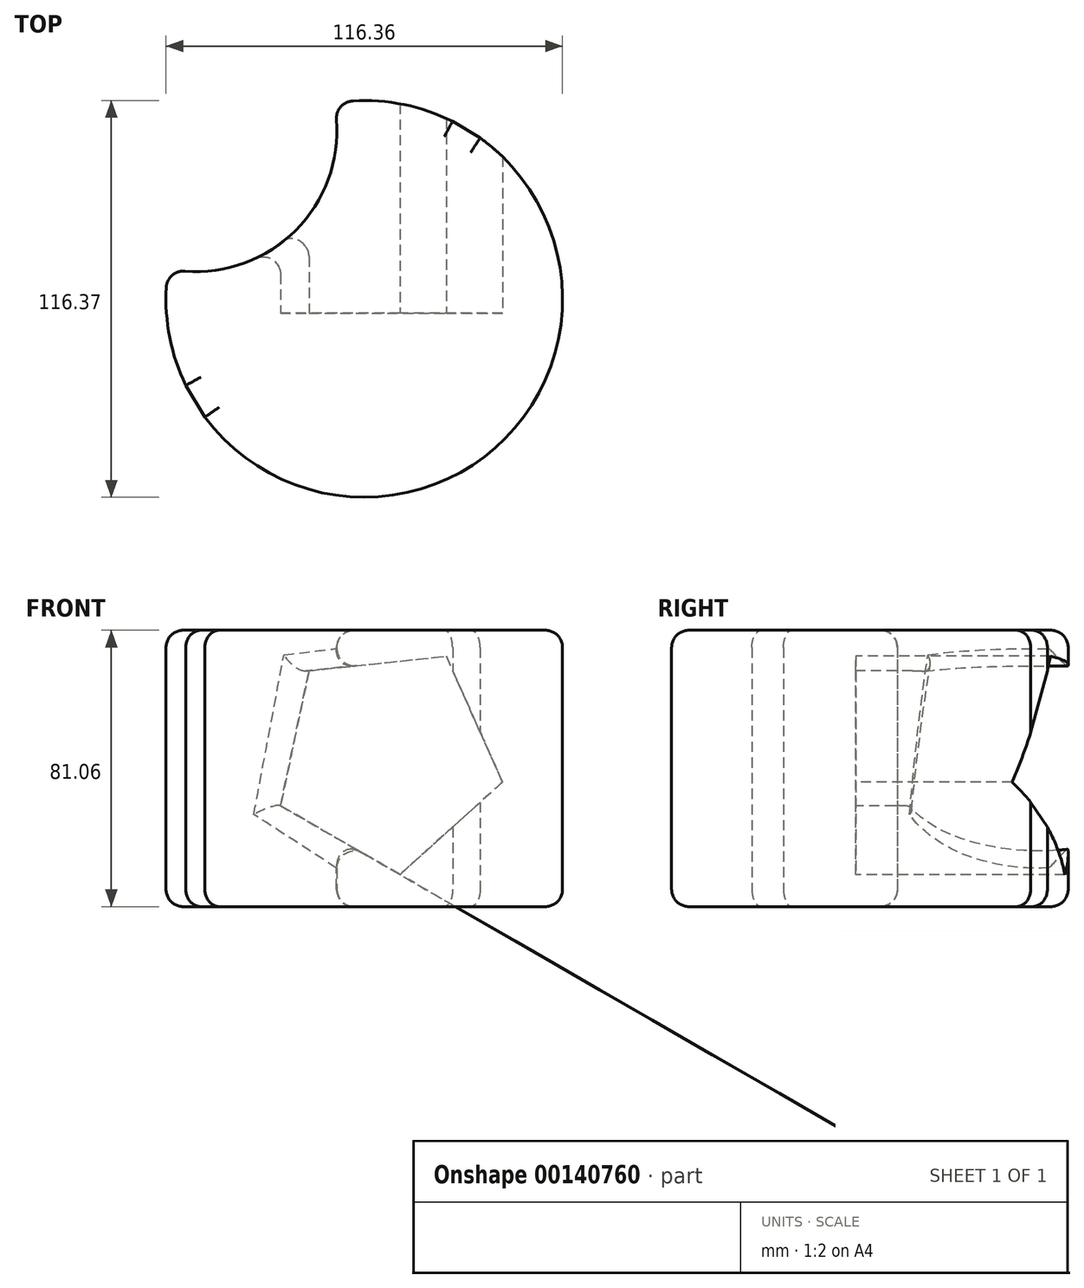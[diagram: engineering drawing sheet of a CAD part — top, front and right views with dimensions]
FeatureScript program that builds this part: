
annotation { "Feature Type Name" : "Feature", "Feature Type Description" : "" }
export const myFeature = defineFeature(function(context is Context, id is Id, definition is map)
    precondition{}
    {
        {
            var Q0;
            Q0=qCreatedBy(makeId("Top.planeOp"),FACE);
            var sketch = newSketch(context, id + "F0", { "sketchPlane" : qUnion([Q0])});
            skCircle(sketch, "E0", {"center": v(-56.15, 53.49) * mm, "radius": 41.28 * mm});
            skCircle(sketch, "E1", {"center": v(-6.85, 4.17) * mm, "radius": 58.18 * mm});
            skLineSegment(sketch, "E2", {"start": v(-33.36, 87.91) * mm, "end": v(27.16, 51.37) * mm});
            skLineSegment(sketch, "E3", {"start": v(-91.43, 32.05) * mm, "end": v(-53.6, -30.47) * mm});
            skSolve(sketch);
        }
        {
            var Q0;
            {var subQ1=sQuery(id+"F0.wireOp",EDGE,"E1");var subQ6=sQuery(id+"F0.wireOp",EDGE,"E0");var subQ9=makeQuery(id+"F0.imprint","INTERSECT",VERTEX,{"disambiguationData":[OD(0.0)],"derivedFrom":[subQ6,subQ1]});Q0=makeQuery(id+"F0.imprint","IMPRINT",FACE,{"disambiguationData":[TD([[makeQuery(id+"F0.imprint","IMPRINT",EDGE,{"disambiguationData":[TD([[subQ9,1.0]])],"derivedFrom":subQ6}),-1.0]])]});}
            extrude(context, id + "F1", {"entities" : qUnion([Q0]), "depth" : 81.06 * mm});
        }
        {
            var Q0;
            Q0=qCreatedBy(makeId("Front.planeOp"),FACE);
            var sketch = newSketch(context, id + "F2", { "sketchPlane" : qUnion([Q0])});
            skCircle(sketch, "E4.cCircle", {"center": v(0, 43.62) * mm, "radius": 27.86 * mm, "construction": true});
            skLineSegment(sketch, "E4.0", {"start": v(33.68, 36.49) * mm, "end": v(3.63, 9.38) * mm});
            skLineSegment(sketch, "E4.1", {"start": v(3.63, 9.38) * mm, "end": v(-31.44, 29.6) * mm});
            skLineSegment(sketch, "E4.2", {"start": v(-31.44, 29.6) * mm, "end": v(-23.06, 69.19) * mm});
            skLineSegment(sketch, "E4.3", {"start": v(-23.06, 69.19) * mm, "end": v(17.2, 73.45) * mm});
            skLineSegment(sketch, "E4.4", {"start": v(17.2, 73.45) * mm, "end": v(33.68, 36.49) * mm});
            skPoint(sketch, "E4.0.midPoint", {"position": v(18.65, 22.93) * mm});
            skSolve(sketch);
        }
        {
            var Q0;
            Q0 = qSketchRegion(id + "F2", true);
            extrude(context, id + "F3", {"entities" : qUnion([Q0]), "operationType" : NewBodyOperationType.REMOVE, "endBound" : BoundingType.THROUGH_ALL, "oppositeDirection" : true, "depth" : 25.4 * mm});
        }
        {
            var Q0;
            Q0=makeQuery(id+"F1.opExtrude","SWEPT_FACE",FACE,{"disambiguationData":[OSD([sQuery(id+"F0.wireOp",EDGE,"E0")])]});
            fillet(context, id + "F4", {"entities" : qUnion([Q0]), "radius" : 5.08 * mm, "tangentPropagation" : true, "allowEdgeOverflow" : false});
        }
        {
            var Q0;
            Q0=makeQuery(id+"F1.opExtrude","CAP_FACE",FACE,{"disambiguationData":[OSD([sQuery(id+"F0.wireOp",EDGE,"E0"),sQuery(id+"F0.wireOp",EDGE,"E1"),sQuery(id+"F0.wireOp",EDGE,"E2"),sQuery(id+"F0.wireOp",EDGE,"E3")])],"isStart":false});
            fillet(context, id + "F5", {"entities" : qUnion([Q0]), "radius" : 5.08 * mm, "tangentPropagation" : true, "allowEdgeOverflow" : false});
        }
        {
            var Q0;
            Q0=makeQuery(id+"F1.opExtrude","CAP_FACE",FACE,{"disambiguationData":[OSD([sQuery(id+"F0.wireOp",EDGE,"E0"),sQuery(id+"F0.wireOp",EDGE,"E1"),sQuery(id+"F0.wireOp",EDGE,"E2"),sQuery(id+"F0.wireOp",EDGE,"E3")])],"isStart":true});
            fillet(context, id + "F6", {"entities" : qUnion([Q0]), "radius" : 5.08 * mm, "tangentPropagation" : true, "allowEdgeOverflow" : false});
        }
    });
